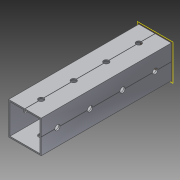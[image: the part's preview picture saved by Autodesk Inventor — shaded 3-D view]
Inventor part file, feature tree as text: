
AUTODESK INVENTOR PART (.ipt)
format: ipt  version: 2014 SP1 (Build 180222100, 222)  size: 1,146,880 bytes
history: native  units: in
note: dims shown in document units (in); Inventor stores cm internally (conversion verified against a paired STEP export)
features: pattern_circular x1, other x1, plane x1, extrude x1, imported_body x1, sketch x1
ambient origin geometry x8: Origin, YZ Plane, XZ Plane, XY Plane, X Axis, Y Axis, Z Axis, Center Point
bodies: Body1 (feature_tree)
feature tree (6):
  pattern_circular  "CirPattern2"
  other  "217-3426-STEP1"
  plane  "Work Plane1"
  extrude  "Extrusion1"  Depth=3937.0079in TaperAngle=0.0deg
  imported_body  "Base1"
  sketch  "Sketch1"  dims[d0=-4.0in d1=3937.0079in d2=0.0in]
